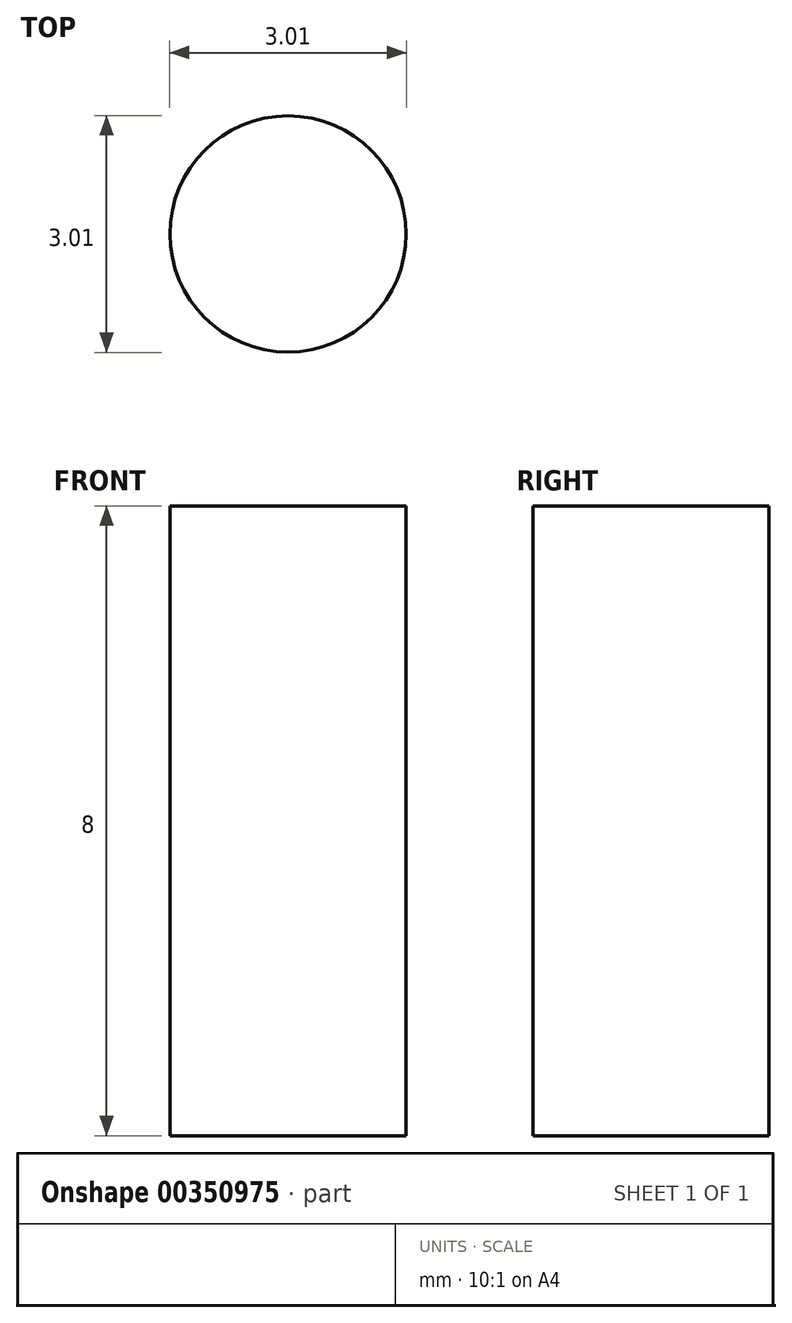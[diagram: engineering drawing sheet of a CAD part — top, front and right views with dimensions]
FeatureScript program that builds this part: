
annotation { "Feature Type Name" : "Feature", "Feature Type Description" : "" }
export const myFeature = defineFeature(function(context is Context, id is Id, definition is map)
    precondition{}
    {
        {
            var Q0;
            Q0=qCreatedBy(makeId("Front.planeOp"),FACE);
            var sketch = newSketch(context, id + "F0", { "sketchPlane" : qUnion([Q0])});
            skLineSegment(sketch, "E0.bottom", {"start": v(-11, 0) * mm, "end": v(11, 0) * mm});
            skLineSegment(sketch, "E0.top", {"start": v(-11, 8) * mm, "end": v(-6.5, 8) * mm});
            skLineSegment(sketch, "E0.left", {"start": v(-11, 0) * mm, "end": v(-11, 8) * mm});
            skLineSegment(sketch, "E0.right", {"start": v(11, 0) * mm, "end": v(11, 8) * mm});
            skLineSegment(sketch, "E1", {"start": v(-6.5, 8) * mm, "end": v(-6.5, 7) * mm});
            skLineSegment(sketch, "E2", {"start": v(-6.5, 7) * mm, "end": v(6.5, 7) * mm});
            skLineSegment(sketch, "E3", {"start": v(6.5, 7) * mm, "end": v(6.5, 8) * mm});
            skLineSegment(sketch, "E4.trimOffspring", {"start": v(6.5, 8) * mm, "end": v(11, 8) * mm});
            skSolve(sketch);
        }
        {
            var Q0;
            Q0=makeQuery(id+"F0.imprint","IMPRINT",FACE,{"disambiguationData":[TD([[makeQuery(id+"F0.imprint","IMPRINT",EDGE,{"derivedFrom":sQuery(id+"F0.wireOp",EDGE,"E0.bottom")}),1.0]])]});
            extrude(context, id + "F1", {"entities" : qUnion([Q0]), "depth" : 4.85 * mm});
        }
        {
            var Q0;
            Q0=makeQuery(id+"F1.opExtrude","SWEPT_FACE",FACE,{"disambiguationData":[OSD([sQuery(id+"F0.wireOp",EDGE,"E0.bottom")])]});
            var sketch = newSketch(context, id + "F2", { "sketchPlane" : qUnion([Q0])});
            skCircle(sketch, "E5", {"center": v(-8.57, 2.43) * mm, "radius": 1.5 * mm});
            skCircle(sketch, "E6.MirrorC", {"center": v(8.57, 2.43) * mm, "radius": 1.5 * mm});
            skSolve(sketch);
        }
        {
            var Q0;
            Q0=makeQuery(id+"F2.imprint","IMPRINT",FACE,{"disambiguationData":[TD([[makeQuery(id+"F2.imprint","IMPRINT",EDGE,{"derivedFrom":sQuery(id+"F2.wireOp",EDGE,"E5")}),1.0]])]});
            var Q1;
            Q1=makeQuery(id+"F2.imprint","IMPRINT",FACE,{"disambiguationData":[TD([[makeQuery(id+"F2.imprint","IMPRINT",EDGE,{"derivedFrom":sQuery(id+"F2.wireOp",EDGE,"E6.MirrorC")}),-1.0]])]});
            extrude(context, id + "F3", {"entities" : qUnion([Q0, Q1]), "operationType" : NewBodyOperationType.REMOVE, "oppositeDirection" : true, "depth" : 10 * mm});
        }
    });
